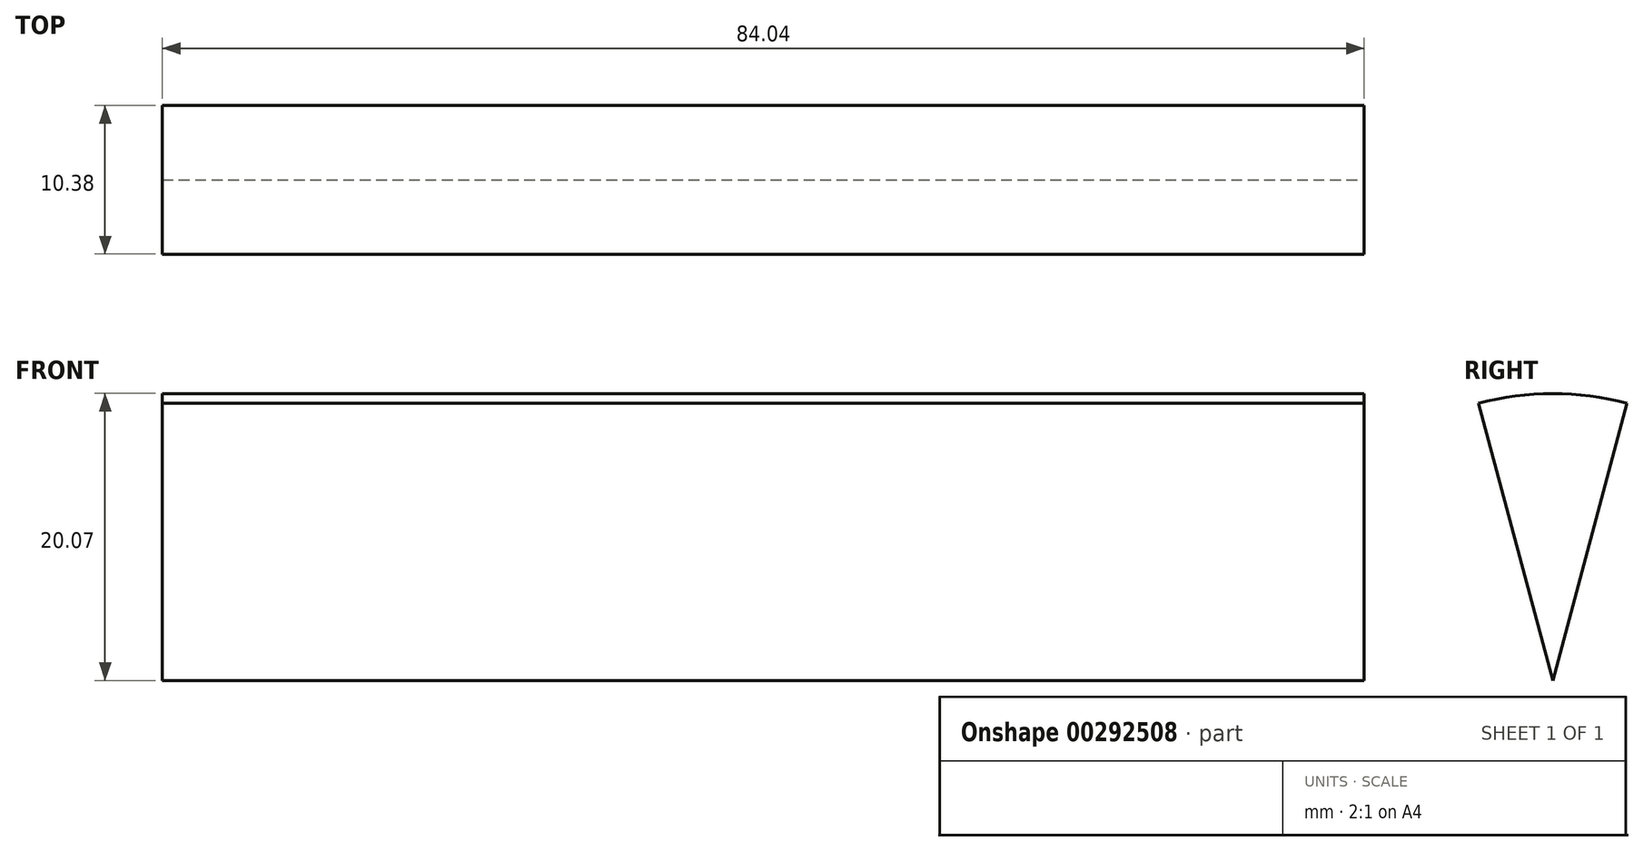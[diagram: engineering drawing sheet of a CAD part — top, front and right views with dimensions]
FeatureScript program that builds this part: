
annotation { "Feature Type Name" : "Feature", "Feature Type Description" : "" }
export const myFeature = defineFeature(function(context is Context, id is Id, definition is map)
    precondition{}
    {
        {
            var Q0;
            Q0=qCreatedBy(makeId("Front.planeOp"),FACE);
            var sketch = newSketch(context, id + "F0", { "sketchPlane" : qUnion([Q0])});
            skLineSegment(sketch, "E0", {"start": v(0, 20.07) * mm, "end": v(42.02, 20.07) * mm});
            skLineSegment(sketch, "E1", {"start": v(42.02, 20.07) * mm, "end": v(42.02, 0) * mm});
            skLineSegment(sketch, "E2.MirrorCS", {"start": v(0, 20.07) * mm, "end": v(-42.02, 20.07) * mm});
            skLineSegment(sketch, "E3.MirrorCS", {"start": v(-42.02, 20.07) * mm, "end": v(-42.02, 0) * mm});
            skLineSegment(sketch, "E4", {"start": v(-42.02, 0) * mm, "end": v(42.02, 0) * mm});
            skSolve(sketch);
        }
        {
            var Q0;
            Q0 = qSketchRegion(id + "F0", true);
            var Q1;
            Q1=sQuery(id+"F0.wireOp",EDGE,"E4");
            revolve(context, id + "F1", {"entities" : qUnion([Q0]), "axis" : qUnion([Q1]), "revolveType" : RevolveType.SYMMETRIC, "angle" : 30 * degree});
        }
    });
